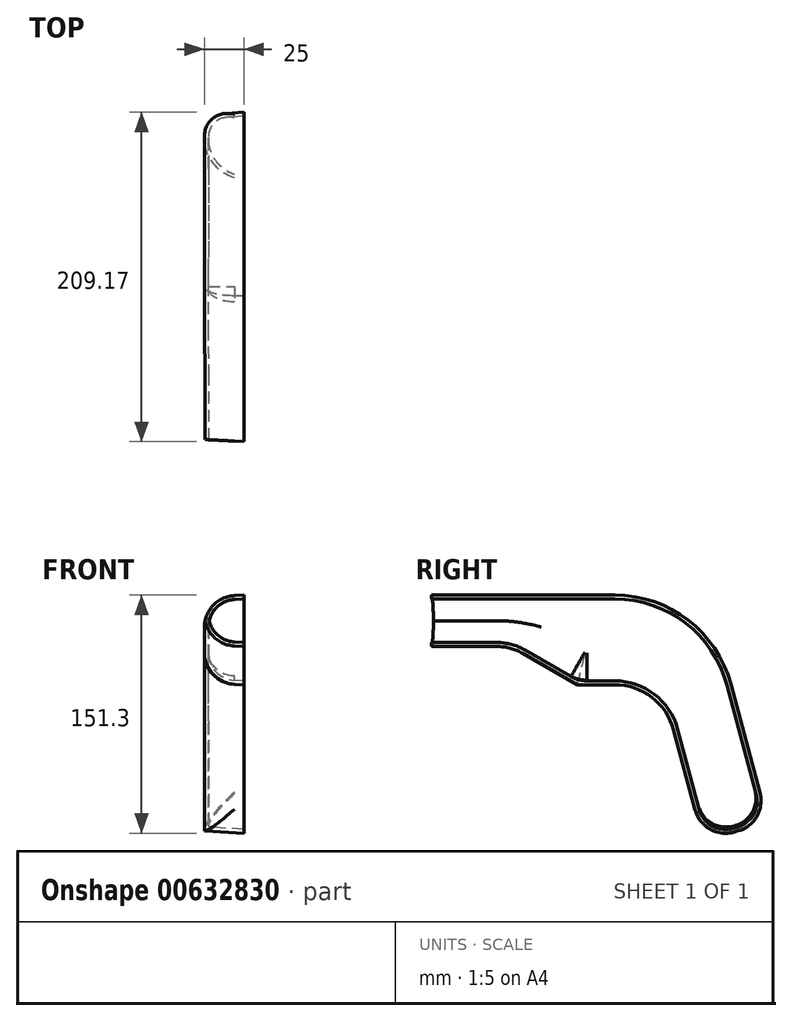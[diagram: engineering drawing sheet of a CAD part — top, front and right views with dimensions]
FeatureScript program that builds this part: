
annotation { "Feature Type Name" : "Feature", "Feature Type Description" : "" }
export const myFeature = defineFeature(function(context is Context, id is Id, definition is map)
    precondition{}
    {
        {
            var Q0;
            Q0=qCreatedBy(makeId("Right.planeOp"),FACE);
            var sketch = newSketch(context, id + "F0", { "sketchPlane" : qUnion([Q0])});
            skLineSegment(sketch, "E0", {"start": v(-115, 64.32) * mm, "end": v(-115, 94.32) * mm});
            skLineSegment(sketch, "E1", {"start": v(-115, 94.32) * mm, "end": v(0, 94.32) * mm});
            skArc(sketch, "E2", {"start": v(72.44, 38.73) * mm, "mid": v(45.66, 78.82) * mm, "end": v(0, 94.32) * mm});
            skLineSegment(sketch, "E3", {"start": v(72.44, 38.73) * mm, "end": v(95.74, -48.2) * mm});
            skLineSegment(sketch, "E4", {"start": v(95.74, -48.2) * mm, "end": v(57.1, -58.56) * mm});
            skLineSegment(sketch, "E5", {"start": v(57.1, -58.56) * mm, "end": v(38.64, 10.35) * mm});
            skArc(sketch, "E6", {"start": v(38.64, 10.35) * mm, "mid": v(24.35, 31.73) * mm, "end": v(0, 40) * mm});
            skLineSegment(sketch, "E7", {"start": v(0, 40) * mm, "end": v(-23.5, 40) * mm});
            skLineSegment(sketch, "E8", {"start": v(-23.5, 40) * mm, "end": v(-57.5, 59.63) * mm});
            skArc(sketch, "E9", {"start": v(-57.5, 59.63) * mm, "mid": v(-65.94, 63.13) * mm, "end": v(-75, 64.32) * mm});
            skLineSegment(sketch, "E10", {"start": v(-75, 64.32) * mm, "end": v(-115, 64.32) * mm});
            skSolve(sketch);
        }
        {
            var Q0;
            Q0 = qSketchRegion(id + "F0", true);
            extrude(context, id + "F1", {"entities" : qUnion([Q0]), "depth" : 25 * mm, "offsetDistance" : 25 * mm, "hasDraft" : true, "draftAngle" : 3 * degree});
        }
        {
            var Q0;
            Q0=makeQuery(id+"F1.opExtrude","CAP_EDGE",EDGE,{"disambiguationData":[OSD([sQuery(id+"F0.wireOp",EDGE,"E2")])],"isStart":true});
            var Q1;
            Q1=makeQuery(id+"F1.opExtrude","CAP_EDGE",EDGE,{"disambiguationData":[OSD([sQuery(id+"F0.wireOp",EDGE,"E9")])],"isStart":true});
            var Q2;
            Q2=makeQuery(id+"F1.opExtrude","CAP_EDGE",EDGE,{"disambiguationData":[OSD([sQuery(id+"F0.wireOp",EDGE,"E10")])],"isStart":true});
            var Q3;
            Q3=makeQuery(id+"F1.opExtrude","CAP_EDGE",EDGE,{"disambiguationData":[OSD([sQuery(id+"F0.wireOp",EDGE,"E8")])],"isStart":true});
            var Q4;
            Q4=makeQuery(id+"F1.opExtrude","CAP_EDGE",EDGE,{"disambiguationData":[OSD([sQuery(id+"F0.wireOp",EDGE,"E7")])],"isStart":true});
            var Q5;
            Q5=makeQuery(id+"F1.opExtrude","SWEPT_EDGE",EDGE,{"disambiguationData":[OSD([sQuery(id+"F0.wireOp",EDGE,"E3"),sQuery(id+"F0.wireOp",EDGE,"E4")])]});
            var Q6;
            Q6=makeQuery(id+"F1.opExtrude","SWEPT_EDGE",EDGE,{"disambiguationData":[OSD([sQuery(id+"F0.wireOp",EDGE,"E4"),sQuery(id+"F0.wireOp",EDGE,"E5")])]});
            fillet(context, id + "F2", {"entities" : qUnion([Q0, Q1, Q2, Q3, Q4, Q5, Q6]), "radius" : 20 * mm, "tangentPropagation" : true, "allowEdgeOverflow" : false});
        }
        {
            var Q0;
            Q0=makeQuery(id+"F1.opExtrude","CAP_FACE",FACE,{"disambiguationData":[OSD([sQuery(id+"F0.wireOp",EDGE,"E0"),sQuery(id+"F0.wireOp",EDGE,"E1"),sQuery(id+"F0.wireOp",EDGE,"E2"),sQuery(id+"F0.wireOp",EDGE,"E3"),sQuery(id+"F0.wireOp",EDGE,"E4"),sQuery(id+"F0.wireOp",EDGE,"E5"),sQuery(id+"F0.wireOp",EDGE,"E6"),sQuery(id+"F0.wireOp",EDGE,"E7"),sQuery(id+"F0.wireOp",EDGE,"E8"),sQuery(id+"F0.wireOp",EDGE,"E9"),sQuery(id+"F0.wireOp",EDGE,"E10")])],"isStart":false});
            var Q1;
            Q1=makeQuery(id+"F1.opExtrude","SWEPT_FACE",FACE,{"disambiguationData":[OSD([sQuery(id+"F0.wireOp",EDGE,"E0")])]});
            shell(context, id + "F3", {"entities" : qUnion([Q0, Q1]), "thickness" : 2.5 * mm});
        }
        {
            var Q0;
            {var subQ0=sQuery(id+"F0.wireOp",EDGE,"E8");var subQ1=sQuery(id+"F0.wireOp",EDGE,"E7");Q0=makeQuery(id+"F3.opShell","OFFSET_EDGE",EDGE,{"disambiguationData":[OSD([subQ1,subQ0]),TDD([makeQuery(id+"F1.opExtrude","SWEPT_EDGE",EDGE,{"disambiguationData":[OSD([subQ1,subQ0])]})])]});}
            fillet(context, id + "F4", {"entities" : qUnion([Q0]), "radius" : 20 * mm, "tangentPropagation" : true, "allowEdgeOverflow" : false});
        }
    });
